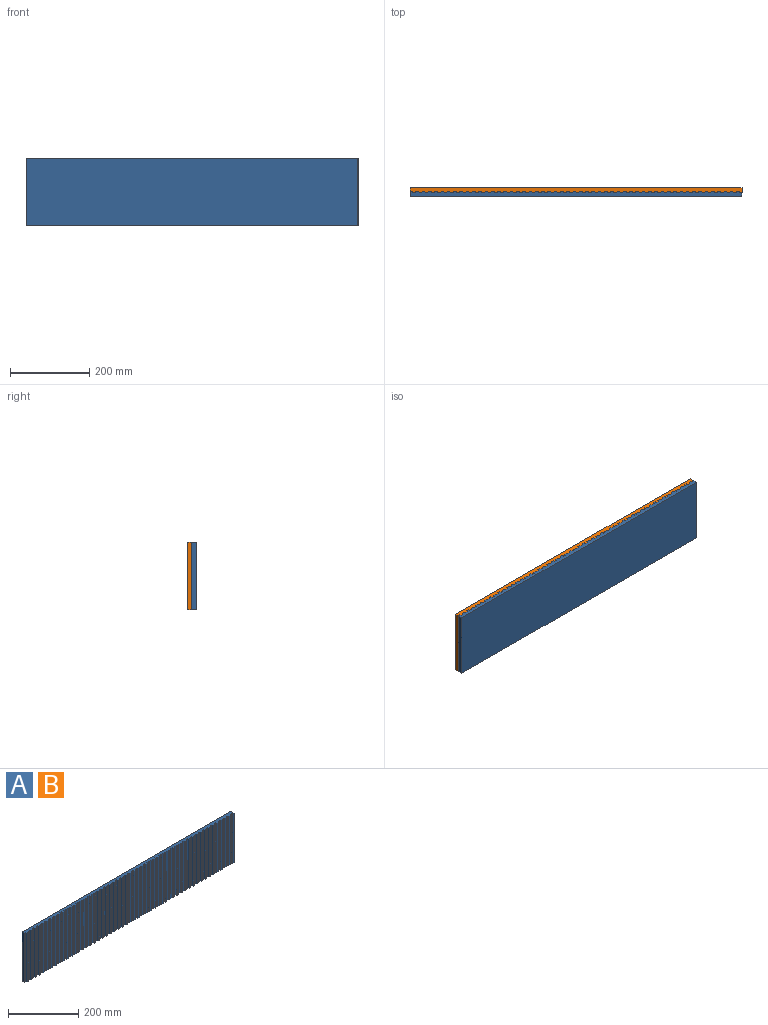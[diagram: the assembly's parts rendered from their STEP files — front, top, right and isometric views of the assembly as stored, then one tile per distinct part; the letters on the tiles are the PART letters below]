
ASSEMBLY  parts=2 mates=1
PART A: 216 faces, bbox 838.2x12.7x171.5 mm
  f0: plane 838.2x171.45mm, normal (0,1,0), area 143709.4mm2, adj f1,f2,f3,f4
  f1: plane 838.2x12.7mm, normal (0,0,1), area 9313mm2, adj f0,f2,f4,f5,f6,f7,f8,f9
  f2: plane 171.45x12.7mm, normal (1,0,0), area 2177.4mm2, adj f0,f1,f3,f173
  f3: plane 838.2x12.7mm, normal (0,0,-1), area 9313mm2, adj f0,f2,f4,f5,f6,f7,f8,f9
  f4: plane 171.45x9.53mm, normal (-1,0,0), area 1633.1mm2, adj f0,f1,f3,f215
  f5: plane 171.45x5.72mm, normal (0,-1,0), area 979.8mm2, adj f1,f3,f6,f174
  f6: plane 171.45x3.18mm, normal (0.82,-0.57,0), area 664.5mm2, adj f1,f3,f5,f7
  f7: plane 171.45x5.72mm, normal (0,-1,0), area 979.8mm2, adj f1,f3,f6,f8
  f8: plane 171.45x3.18mm, normal (-0.82,-0.57,0), area 664.5mm2, adj f1,f3,f7,f9
  f9: plane 171.45x5.72mm, normal (0,-1,0), area 979.8mm2, adj f1,f3,f8,f10
  f10: plane 171.45x3.18mm, normal (0.82,-0.57,0), area 664.5mm2, adj f1,f3,f9,f11
  f11: plane 171.45x5.72mm, normal (0,-1,0), area 979.8mm2, adj f1,f3,f10,f12
  f12: plane 171.45x3.18mm, normal (-0.82,-0.57,0), area 664.5mm2, adj f1,f3,f11,f13
  f13: plane 171.45x5.72mm, normal (0,-1,0), area 979.8mm2, adj f1,f3,f12,f14
  f14: plane 171.45x3.18mm, normal (0.82,-0.57,0), area 664.5mm2, adj f1,f3,f13,f15
  f15: plane 171.45x5.72mm, normal (0,-1,0), area 979.8mm2, adj f1,f3,f14,f16
  f16: plane 171.45x3.18mm, normal (-0.82,-0.57,0), area 664.5mm2, adj f1,f3,f15,f17
  f17: plane 171.45x5.72mm, normal (0,-1,0), area 979.8mm2, adj f1,f3,f16,f18
  f18: plane 171.45x3.18mm, normal (0.82,-0.57,0), area 664.5mm2, adj f1,f3,f17,f19
  f19: plane 171.45x5.72mm, normal (0,-1,0), area 979.8mm2, adj f1,f3,f18,f20
  f20: plane 171.45x3.18mm, normal (-0.82,-0.57,0), area 664.5mm2, adj f1,f3,f19,f21
  f21: plane 171.45x5.72mm, normal (0,-1,0), area 979.8mm2, adj f1,f3,f20,f22
  f22: plane 171.45x3.18mm, normal (0.82,-0.57,0), area 664.5mm2, adj f1,f3,f21,f23
  f23: plane 171.45x5.72mm, normal (0,-1,0), area 979.8mm2, adj f1,f3,f22,f24
  f24: plane 171.45x3.18mm, normal (-0.82,-0.57,0), area 664.5mm2, adj f1,f3,f23,f25
  f25: plane 171.45x5.72mm, normal (0,-1,0), area 979.8mm2, adj f1,f3,f24,f26
  f26: plane 171.45x3.18mm, normal (0.82,-0.57,0), area 664.5mm2, adj f1,f3,f25,f27
  f27: plane 171.45x5.72mm, normal (0,-1,0), area 979.8mm2, adj f1,f3,f26,f28
  f28: plane 171.45x3.18mm, normal (-0.82,-0.57,0), area 664.5mm2, adj f1,f3,f27,f29
  f29: plane 171.45x5.72mm, normal (0,-1,0), area 979.8mm2, adj f1,f3,f28,f30
  f30: plane 171.45x3.18mm, normal (0.82,-0.57,0), area 664.5mm2, adj f1,f3,f29,f31
  f31: plane 171.45x5.72mm, normal (0,-1,0), area 979.8mm2, adj f1,f3,f30,f32
  f32: plane 171.45x3.18mm, normal (-0.82,-0.57,0), area 664.5mm2, adj f1,f3,f31,f33
  f33: plane 171.45x5.72mm, normal (0,-1,0), area 979.8mm2, adj f1,f3,f32,f34
  f34: plane 171.45x3.18mm, normal (0.82,-0.57,0), area 664.5mm2, adj f1,f3,f33,f35
  f35: plane 171.45x5.72mm, normal (0,-1,0), area 979.8mm2, adj f1,f3,f34,f36
  f36: plane 171.45x3.18mm, normal (-0.82,-0.57,0), area 664.5mm2, adj f1,f3,f35,f37
  f37: plane 171.45x5.72mm, normal (0,-1,0), area 979.8mm2, adj f1,f3,f36,f38
  f38: plane 171.45x3.18mm, normal (0.82,-0.57,0), area 664.5mm2, adj f1,f3,f37,f39
  f39: plane 171.45x5.72mm, normal (0,-1,0), area 979.8mm2, adj f1,f3,f38,f40
  f40: plane 171.45x3.18mm, normal (-0.82,-0.57,0), area 664.5mm2, adj f1,f3,f39,f41
  f41: plane 171.45x5.72mm, normal (0,-1,0), area 979.8mm2, adj f1,f3,f40,f42
  f42: plane 171.45x3.18mm, normal (0.82,-0.57,0), area 664.5mm2, adj f1,f3,f41,f43
  f43: plane 171.45x5.72mm, normal (0,-1,0), area 979.8mm2, adj f1,f3,f42,f44
  f44: plane 171.45x3.18mm, normal (-0.82,-0.57,0), area 664.5mm2, adj f1,f3,f43,f45
  f45: plane 171.45x5.72mm, normal (0,-1,0), area 979.8mm2, adj f1,f3,f44,f46
  f46: plane 171.45x3.18mm, normal (0.82,-0.57,0), area 664.5mm2, adj f1,f3,f45,f47
  f47: plane 171.45x5.72mm, normal (0,-1,0), area 979.8mm2, adj f1,f3,f46,f48
  f48: plane 171.45x3.18mm, normal (-0.82,-0.57,0), area 664.5mm2, adj f1,f3,f47,f49
  f49: plane 171.45x5.72mm, normal (0,-1,0), area 979.8mm2, adj f1,f3,f48,f50
  f50: plane 171.45x3.18mm, normal (0.82,-0.57,0), area 664.5mm2, adj f1,f3,f49,f51
  f51: plane 171.45x5.72mm, normal (0,-1,0), area 979.8mm2, adj f1,f3,f50,f52
  f52: plane 171.45x3.18mm, normal (-0.82,-0.57,0), area 664.5mm2, adj f1,f3,f51,f53
  f53: plane 171.45x5.72mm, normal (0,-1,0), area 979.8mm2, adj f1,f3,f52,f54
  f54: plane 171.45x3.18mm, normal (0.82,-0.57,0), area 664.5mm2, adj f1,f3,f53,f55
  f55: plane 171.45x5.72mm, normal (0,-1,0), area 979.8mm2, adj f1,f3,f54,f56
  f56: plane 171.45x3.18mm, normal (-0.82,-0.57,0), area 664.5mm2, adj f1,f3,f55,f57
  f57: plane 171.45x5.72mm, normal (0,-1,0), area 979.8mm2, adj f1,f3,f56,f58
  f58: plane 171.45x3.18mm, normal (0.82,-0.57,0), area 664.5mm2, adj f1,f3,f57,f59
  f59: plane 171.45x5.72mm, normal (0,-1,0), area 979.8mm2, adj f1,f3,f58,f60
  f60: plane 171.45x3.18mm, normal (-0.82,-0.57,0), area 664.5mm2, adj f1,f3,f59,f61
  f61: plane 171.45x5.72mm, normal (0,-1,0), area 979.8mm2, adj f1,f3,f60,f62
  f62: plane 171.45x3.18mm, normal (0.82,-0.57,0), area 664.5mm2, adj f1,f3,f61,f63
  f63: plane 171.45x5.72mm, normal (0,-1,0), area 979.8mm2, adj f1,f3,f62,f64
  f64: plane 171.45x3.18mm, normal (-0.82,-0.57,0), area 664.5mm2, adj f1,f3,f63,f65
  f65: plane 171.45x5.72mm, normal (0,-1,0), area 979.8mm2, adj f1,f3,f64,f66
  f66: plane 171.45x3.18mm, normal (0.82,-0.57,0), area 664.5mm2, adj f1,f3,f65,f67
  f67: plane 171.45x5.72mm, normal (0,-1,0), area 979.8mm2, adj f1,f3,f66,f68
  f68: plane 171.45x3.18mm, normal (-0.82,-0.57,0), area 664.5mm2, adj f1,f3,f67,f69
  f69: plane 171.45x5.72mm, normal (0,-1,0), area 979.8mm2, adj f1,f3,f68,f70
  f70: plane 171.45x3.18mm, normal (0.82,-0.57,0), area 664.5mm2, adj f1,f3,f69,f71
  f71: plane 171.45x5.72mm, normal (0,-1,0), area 979.8mm2, adj f1,f3,f70,f72
  f72: plane 171.45x3.18mm, normal (-0.82,-0.57,0), area 664.5mm2, adj f1,f3,f71,f73
  f73: plane 171.45x5.72mm, normal (0,-1,0), area 979.8mm2, adj f1,f3,f72,f74
  f74: plane 171.45x3.18mm, normal (0.82,-0.57,0), area 664.5mm2, adj f1,f3,f73,f75
  f75: plane 171.45x5.72mm, normal (0,-1,0), area 979.8mm2, adj f1,f3,f74,f76
  f76: plane 171.45x3.18mm, normal (-0.82,-0.57,0), area 664.5mm2, adj f1,f3,f75,f77
  f77: plane 171.45x5.72mm, normal (0,-1,0), area 979.8mm2, adj f1,f3,f76,f78
  f78: plane 171.45x3.18mm, normal (0.82,-0.57,0), area 664.5mm2, adj f1,f3,f77,f79
  f79: plane 171.45x5.72mm, normal (0,-1,0), area 979.8mm2, adj f1,f3,f78,f80
  f80: plane 171.45x3.18mm, normal (-0.82,-0.57,0), area 664.5mm2, adj f1,f3,f79,f81
  f81: plane 171.45x5.72mm, normal (0,-1,0), area 979.8mm2, adj f1,f3,f80,f82
  f82: plane 171.45x3.18mm, normal (0.82,-0.57,0), area 664.5mm2, adj f1,f3,f81,f83
  f83: plane 171.45x5.72mm, normal (0,-1,0), area 979.8mm2, adj f1,f3,f82,f84
  f84: plane 171.45x3.18mm, normal (-0.82,-0.57,0), area 664.5mm2, adj f1,f3,f83,f85
  f85: plane 171.45x5.72mm, normal (0,-1,0), area 979.8mm2, adj f1,f3,f84,f86
  f86: plane 171.45x3.18mm, normal (0.82,-0.57,0), area 664.5mm2, adj f1,f3,f85,f87
  f87: plane 171.45x5.72mm, normal (0,-1,0), area 979.8mm2, adj f1,f3,f86,f88
  f88: plane 171.45x3.18mm, normal (-0.82,-0.57,0), area 664.5mm2, adj f1,f3,f87,f89
  f89: plane 171.45x5.72mm, normal (0,-1,0), area 979.8mm2, adj f1,f3,f88,f90
  f90: plane 171.45x3.18mm, normal (0.82,-0.57,0), area 664.5mm2, adj f1,f3,f89,f91
  f91: plane 171.45x5.72mm, normal (0,-1,0), area 979.8mm2, adj f1,f3,f90,f92
  f92: plane 171.45x3.18mm, normal (-0.82,-0.57,0), area 664.5mm2, adj f1,f3,f91,f93
  f93: plane 171.45x5.72mm, normal (0,-1,0), area 979.8mm2, adj f1,f3,f92,f94
  f94: plane 171.45x3.18mm, normal (0.82,-0.57,0), area 664.5mm2, adj f1,f3,f93,f95
  f95: plane 171.45x5.72mm, normal (0,-1,0), area 979.8mm2, adj f1,f3,f94,f96
  f96: plane 171.45x3.18mm, normal (-0.82,-0.57,0), area 664.5mm2, adj f1,f3,f95,f97
  f97: plane 171.45x5.72mm, normal (0,-1,0), area 979.8mm2, adj f1,f3,f96,f98
  f98: plane 171.45x3.18mm, normal (0.82,-0.57,0), area 664.5mm2, adj f1,f3,f97,f99
  f99: plane 171.45x5.72mm, normal (0,-1,0), area 979.8mm2, adj f1,f3,f98,f100
  f100: plane 171.45x3.18mm, normal (-0.82,-0.57,0), area 664.5mm2, adj f1,f3,f99,f101
  f101: plane 171.45x5.72mm, normal (0,-1,0), area 979.8mm2, adj f1,f3,f100,f102
  f102: plane 171.45x3.18mm, normal (0.82,-0.57,0), area 664.5mm2, adj f1,f3,f101,f103
  f103: plane 171.45x5.72mm, normal (0,-1,0), area 979.8mm2, adj f1,f3,f102,f104
  f104: plane 171.45x3.18mm, normal (-0.82,-0.57,0), area 664.5mm2, adj f1,f3,f103,f105
  f105: plane 171.45x5.72mm, normal (0,-1,0), area 979.8mm2, adj f1,f3,f104,f106
  f106: plane 171.45x3.18mm, normal (0.82,-0.57,0), area 664.5mm2, adj f1,f3,f105,f107
  f107: plane 171.45x5.72mm, normal (0,-1,0), area 979.8mm2, adj f1,f3,f106,f108
  f108: plane 171.45x3.18mm, normal (-0.82,-0.57,0), area 664.5mm2, adj f1,f3,f107,f109
  f109: plane 171.45x5.72mm, normal (0,-1,0), area 979.8mm2, adj f1,f3,f108,f110
  f110: plane 171.45x3.18mm, normal (0.82,-0.57,0), area 664.5mm2, adj f1,f3,f109,f111
  f111: plane 171.45x5.72mm, normal (0,-1,0), area 979.8mm2, adj f1,f3,f110,f112
  f112: plane 171.45x3.18mm, normal (-0.82,-0.57,0), area 664.5mm2, adj f1,f3,f111,f113
  f113: plane 171.45x5.72mm, normal (0,-1,0), area 979.8mm2, adj f1,f3,f112,f114
  f114: plane 171.45x3.18mm, normal (0.82,-0.57,0), area 664.5mm2, adj f1,f3,f113,f115
  f115: plane 171.45x5.72mm, normal (0,-1,0), area 979.8mm2, adj f1,f3,f114,f116
  f116: plane 171.45x3.18mm, normal (-0.82,-0.57,0), area 664.5mm2, adj f1,f3,f115,f117
  f117: plane 171.45x5.72mm, normal (0,-1,0), area 979.8mm2, adj f1,f3,f116,f118
  f118: plane 171.45x3.18mm, normal (0.82,-0.57,0), area 664.5mm2, adj f1,f3,f117,f119
  f119: plane 171.45x5.72mm, normal (0,-1,0), area 979.8mm2, adj f1,f3,f118,f120
  f120: plane 171.45x3.18mm, normal (-0.82,-0.57,0), area 664.5mm2, adj f1,f3,f119,f121
  f121: plane 171.45x5.72mm, normal (0,-1,0), area 979.8mm2, adj f1,f3,f120,f122
  f122: plane 171.45x3.18mm, normal (0.82,-0.57,0), area 664.5mm2, adj f1,f3,f121,f123
  f123: plane 171.45x5.72mm, normal (0,-1,0), area 979.8mm2, adj f1,f3,f122,f124
  f124: plane 171.45x3.18mm, normal (-0.82,-0.57,0), area 664.5mm2, adj f1,f3,f123,f125
  f125: plane 171.45x5.72mm, normal (0,-1,0), area 979.8mm2, adj f1,f3,f124,f126
  f126: plane 171.45x3.18mm, normal (0.82,-0.57,0), area 664.5mm2, adj f1,f3,f125,f127
  f127: plane 171.45x5.72mm, normal (0,-1,0), area 979.8mm2, adj f1,f3,f126,f128
  f128: plane 171.45x3.18mm, normal (-0.82,-0.57,0), area 664.5mm2, adj f1,f3,f127,f129
  f129: plane 171.45x5.72mm, normal (0,-1,0), area 979.8mm2, adj f1,f3,f128,f130
  f130: plane 171.45x3.18mm, normal (0.82,-0.57,0), area 664.5mm2, adj f1,f3,f129,f131
  f131: plane 171.45x5.72mm, normal (0,-1,0), area 979.8mm2, adj f1,f3,f130,f132
  f132: plane 171.45x3.18mm, normal (-0.82,-0.57,0), area 664.5mm2, adj f1,f3,f131,f133
  f133: plane 171.45x5.72mm, normal (0,-1,0), area 979.8mm2, adj f1,f3,f132,f134
  f134: plane 171.45x3.18mm, normal (0.82,-0.57,0), area 664.5mm2, adj f1,f3,f133,f135
  f135: plane 171.45x5.72mm, normal (0,-1,0), area 979.8mm2, adj f1,f3,f134,f136
  f136: plane 171.45x3.18mm, normal (-0.82,-0.57,0), area 664.5mm2, adj f1,f3,f135,f137
  f137: plane 171.45x5.72mm, normal (0,-1,0), area 979.8mm2, adj f1,f3,f136,f138
  f138: plane 171.45x3.18mm, normal (0.82,-0.57,0), area 664.5mm2, adj f1,f3,f137,f139
  f139: plane 171.45x5.72mm, normal (0,-1,0), area 979.8mm2, adj f1,f3,f138,f140
  f140: plane 171.45x3.18mm, normal (-0.82,-0.57,0), area 664.5mm2, adj f1,f3,f139,f141
  f141: plane 171.45x5.72mm, normal (0,-1,0), area 979.8mm2, adj f1,f3,f140,f142
  f142: plane 171.45x3.18mm, normal (0.82,-0.57,0), area 664.5mm2, adj f1,f3,f141,f143
  f143: plane 171.45x5.72mm, normal (0,-1,0), area 979.8mm2, adj f1,f3,f142,f144
  f144: plane 171.45x3.18mm, normal (-0.82,-0.57,0), area 664.5mm2, adj f1,f3,f143,f145
  f145: plane 171.45x5.72mm, normal (0,-1,0), area 979.8mm2, adj f1,f3,f144,f146
  f146: plane 171.45x3.18mm, normal (0.82,-0.57,0), area 664.5mm2, adj f1,f3,f145,f147
  f147: plane 171.45x5.72mm, normal (0,-1,0), area 979.8mm2, adj f1,f3,f146,f148
  f148: plane 171.45x3.18mm, normal (-0.82,-0.57,0), area 664.5mm2, adj f1,f3,f147,f149
  f149: plane 171.45x5.72mm, normal (0,-1,0), area 979.8mm2, adj f1,f3,f148,f150
  f150: plane 171.45x3.18mm, normal (0.82,-0.57,0), area 664.5mm2, adj f1,f3,f149,f151
  f151: plane 171.45x5.72mm, normal (0,-1,0), area 979.8mm2, adj f1,f3,f150,f152
  f152: plane 171.45x3.18mm, normal (-0.82,-0.57,0), area 664.5mm2, adj f1,f3,f151,f153
  f153: plane 171.45x5.72mm, normal (0,-1,0), area 979.8mm2, adj f1,f3,f152,f154
  f154: plane 171.45x3.18mm, normal (0.82,-0.57,0), area 664.5mm2, adj f1,f3,f153,f155
  f155: plane 171.45x5.72mm, normal (0,-1,0), area 979.8mm2, adj f1,f3,f154,f156
  f156: plane 171.45x3.18mm, normal (-0.82,-0.57,0), area 664.5mm2, adj f1,f3,f155,f157
  f157: plane 171.45x5.72mm, normal (0,-1,0), area 979.8mm2, adj f1,f3,f156,f158
  f158: plane 171.45x3.18mm, normal (0.82,-0.57,0), area 664.5mm2, adj f1,f3,f157,f159
  f159: plane 171.45x5.72mm, normal (0,-1,0), area 979.8mm2, adj f1,f3,f158,f160
  f160: plane 171.45x3.18mm, normal (-0.82,-0.57,0), area 664.5mm2, adj f1,f3,f159,f161
  f161: plane 171.45x5.72mm, normal (0,-1,0), area 979.8mm2, adj f1,f3,f160,f162
  f162: plane 171.45x3.18mm, normal (0.82,-0.57,0), area 664.5mm2, adj f1,f3,f161,f163
  f163: plane 171.45x5.72mm, normal (0,-1,0), area 979.8mm2, adj f1,f3,f162,f164
  f164: plane 171.45x3.18mm, normal (-0.82,-0.57,0), area 664.5mm2, adj f1,f3,f163,f165
  f165: plane 171.45x5.72mm, normal (0,-1,0), area 979.8mm2, adj f1,f3,f164,f166
  f166: plane 171.45x3.18mm, normal (0.82,-0.57,0), area 664.5mm2, adj f1,f3,f165,f167
  f167: plane 171.45x5.72mm, normal (0,-1,0), area 979.8mm2, adj f1,f3,f166,f168
  f168: plane 171.45x3.18mm, normal (-0.82,-0.57,0), area 664.5mm2, adj f1,f3,f167,f169
  f169: plane 171.45x5.72mm, normal (0,-1,0), area 979.8mm2, adj f1,f3,f168,f170
  f170: plane 171.45x3.18mm, normal (0.82,-0.57,0), area 664.5mm2, adj f1,f3,f169,f171
  f171: plane 171.45x5.72mm, normal (0,-1,0), area 979.8mm2, adj f1,f3,f170,f172
  f172: plane 171.45x3.18mm, normal (-0.82,-0.57,0), area 664.5mm2, adj f1,f3,f171,f173
  f173: plane 171.45x4.76mm, normal (0,-1,0), area 816.5mm2, adj f1,f2,f3,f172
  f174: plane 171.45x3.18mm, normal (-0.82,-0.57,0), area 664.5mm2, adj f1,f3,f5,f175
  f175: plane 171.45x5.72mm, normal (0,-1,0), area 979.8mm2, adj f1,f3,f174,f176
  f176: plane 171.45x3.18mm, normal (0.82,-0.57,0), area 664.5mm2, adj f1,f3,f175,f177
  f177: plane 171.45x5.72mm, normal (0,-1,0), area 979.8mm2, adj f1,f3,f176,f178
  f178: plane 171.45x3.18mm, normal (-0.82,-0.57,0), area 664.5mm2, adj f1,f3,f177,f179
  f179: plane 171.45x5.72mm, normal (0,-1,0), area 979.8mm2, adj f1,f3,f178,f180
  f180: plane 171.45x3.18mm, normal (0.82,-0.57,0), area 664.5mm2, adj f1,f3,f179,f181
  f181: plane 171.45x5.72mm, normal (0,-1,0), area 979.8mm2, adj f1,f3,f180,f182
  f182: plane 171.45x3.18mm, normal (-0.82,-0.57,0), area 664.5mm2, adj f1,f3,f181,f183
  f183: plane 171.45x5.72mm, normal (0,-1,0), area 979.8mm2, adj f1,f3,f182,f184
  f184: plane 171.45x3.18mm, normal (0.82,-0.57,0), area 664.5mm2, adj f1,f3,f183,f185
  f185: plane 171.45x5.72mm, normal (0,-1,0), area 979.8mm2, adj f1,f3,f184,f186
  f186: plane 171.45x3.18mm, normal (-0.82,-0.57,0), area 664.5mm2, adj f1,f3,f185,f187
  f187: plane 171.45x5.72mm, normal (0,-1,0), area 979.8mm2, adj f1,f3,f186,f188
  f188: plane 171.45x3.18mm, normal (0.82,-0.57,0), area 664.5mm2, adj f1,f3,f187,f189
  f189: plane 171.45x5.72mm, normal (0,-1,0), area 979.8mm2, adj f1,f3,f188,f190
  f190: plane 171.45x3.18mm, normal (-0.82,-0.57,0), area 664.5mm2, adj f1,f3,f189,f191
  f191: plane 171.45x5.72mm, normal (0,-1,0), area 979.8mm2, adj f1,f3,f190,f192
  f192: plane 171.45x3.18mm, normal (0.82,-0.57,0), area 664.5mm2, adj f1,f3,f191,f193
  f193: plane 171.45x5.72mm, normal (0,-1,0), area 979.8mm2, adj f1,f3,f192,f194
  f194: plane 171.45x3.18mm, normal (-0.82,-0.57,0), area 664.5mm2, adj f1,f3,f193,f195
  f195: plane 171.45x5.72mm, normal (0,-1,0), area 979.8mm2, adj f1,f3,f194,f196
  f196: plane 171.45x3.18mm, normal (0.82,-0.57,0), area 664.5mm2, adj f1,f3,f195,f197
  f197: plane 171.45x5.72mm, normal (0,-1,0), area 979.8mm2, adj f1,f3,f196,f198
  f198: plane 171.45x3.18mm, normal (-0.82,-0.57,0), area 664.5mm2, adj f1,f3,f197,f199
  f199: plane 171.45x5.72mm, normal (0,-1,0), area 979.8mm2, adj f1,f3,f198,f200
  f200: plane 171.45x3.18mm, normal (0.82,-0.57,0), area 664.5mm2, adj f1,f3,f199,f201
  f201: plane 171.45x5.72mm, normal (0,-1,0), area 979.8mm2, adj f1,f3,f200,f202
  f202: plane 171.45x3.18mm, normal (-0.82,-0.57,0), area 664.5mm2, adj f1,f3,f201,f203
  f203: plane 171.45x5.72mm, normal (0,-1,0), area 979.8mm2, adj f1,f3,f202,f204
  f204: plane 171.45x3.18mm, normal (0.82,-0.57,0), area 664.5mm2, adj f1,f3,f203,f205
  f205: plane 171.45x5.72mm, normal (0,-1,0), area 979.8mm2, adj f1,f3,f204,f206
  f206: plane 171.45x3.18mm, normal (-0.82,-0.57,0), area 664.5mm2, adj f1,f3,f205,f207
  f207: plane 171.45x5.72mm, normal (0,-1,0), area 979.8mm2, adj f1,f3,f206,f208
  f208: plane 171.45x3.18mm, normal (0.82,-0.57,0), area 664.5mm2, adj f1,f3,f207,f209
  f209: plane 171.45x5.72mm, normal (0,-1,0), area 979.8mm2, adj f1,f3,f208,f210
  f210: plane 171.45x3.18mm, normal (-0.82,-0.57,0), area 664.5mm2, adj f1,f3,f209,f211
  f211: plane 171.45x5.72mm, normal (0,-1,0), area 979.8mm2, adj f1,f3,f210,f212
  f212: plane 171.45x3.18mm, normal (0.82,-0.57,0), area 664.5mm2, adj f1,f3,f211,f213
  f213: plane 171.45x5.72mm, normal (0,-1,0), area 979.8mm2, adj f1,f3,f212,f214
  f214: plane 171.45x3.18mm, normal (-0.82,-0.57,0), area 664.5mm2, adj f1,f3,f213,f215
  f215: plane 171.45x5.72mm, normal (0,-1,0), area 979.8mm2, adj f1,f3,f4,f214
PART B: same geometry as A
PLACE A rot(axis=(0,0,-1),180deg) t=(-432.28,-234.44,-29.32)mm
PLACE B t=(-1125.94,-212.22,-29.32)mm
MATE fastened B.f215 <-> A.f173  axis (0,-1,0) through (-1198.21,-221.74,-115.23)mm
